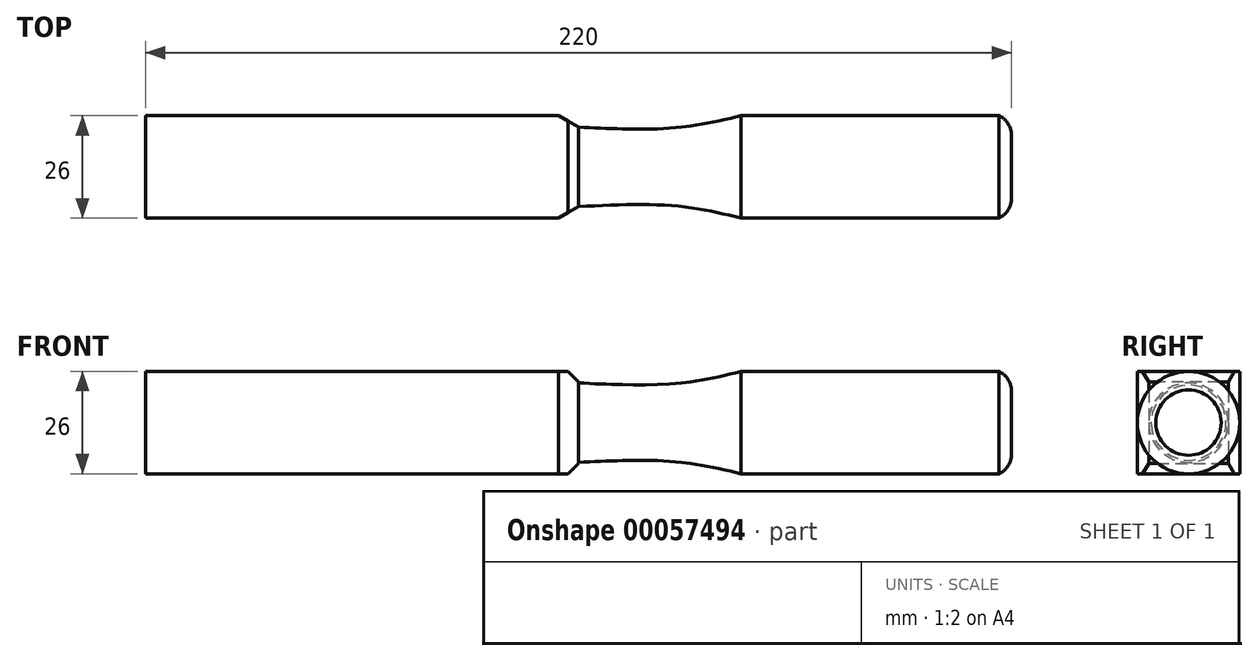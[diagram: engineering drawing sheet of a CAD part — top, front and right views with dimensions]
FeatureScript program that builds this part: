
annotation { "Feature Type Name" : "Feature", "Feature Type Description" : "" }
export const myFeature = defineFeature(function(context is Context, id is Id, definition is map)
    precondition{}
    {
        {
            var Q0;
            Q0=qCreatedBy(makeId("Top.planeOp"),FACE);
            var sketch = newSketch(context, id + "F0", { "sketchPlane" : qUnion([Q0])});
            skLineSegment(sketch, "E0", {"start": v(-89.28, 0) * mm, "end": v(131.67, 0) * mm, "construction": true});
            skLineSegment(sketch, "E1", {"start": v(0, 12.04) * mm, "end": v(0, -13) * mm, "construction": true});
            skLineSegment(sketch, "E2.0", {"start": v(-89.28, -13) * mm, "end": v(131.67, -13) * mm, "construction": true});
            skLineSegment(sketch, "E3.0", {"start": v(-89.28, 13) * mm, "end": v(131.67, 13) * mm, "construction": true});
            skLineSegment(sketch, "E4", {"start": v(0, 13) * mm, "end": v(0, -13) * mm});
            skLineSegment(sketch, "E5.0", {"start": v(-110, 13) * mm, "end": v(-110, -13) * mm});
            skLineSegment(sketch, "E6.0", {"start": v(110, 13) * mm, "end": v(110, -13) * mm});
            skLineSegment(sketch, "E7", {"start": v(-110, -13) * mm, "end": v(0, -13) * mm});
            skLineSegment(sketch, "E8", {"start": v(0, 13) * mm, "end": v(-110, 13) * mm});
            skFitSpline(sketch, "E9", {"points": [v(0, -10.1) * mm, v(24.61, -9.92) * mm, v(41.35, -13) * mm], "startDerivative": vector(47.32, 2.24) * mm, "endDerivative": vector(35, -8.38) * mm});
            skArc(sketch, "E10", {"start": v(106.8, -13) * mm, "mid": v(109.18, -10.95) * mm, "end": v(110, -7.92) * mm});
            skLineSegment(sketch, "E11", {"start": v(41.35, -13) * mm, "end": v(106.8, -13) * mm});
            skLineSegment(sketch, "E12", {"start": v(0, 0) * mm, "end": v(110, 0) * mm});
            skLineSegment(sketch, "E13.0", {"start": v(-5, 13) * mm, "end": v(-5, -13) * mm});
            skLineSegment(sketch, "E14", {"start": v(0, -10.1) * mm, "end": v(-5, -13) * mm});
            skLineSegment(sketch, "E15.MirrorCS", {"start": v(0, 10.1) * mm, "end": v(-5, 13) * mm});
            skSolve(sketch);
        }
        {
            var Q0;
            {var subQ0=sQuery(id+"F0.wireOp",EDGE,"E9");Q0=makeQuery(id+"F0.imprint","IMPRINT",FACE,{"disambiguationData":[TD([[makeQuery(id+"F0.imprint","IMPRINT",EDGE,{"derivedFrom":subQ0}),1.0]])]});}
            var Q1;
            Q1=sQuery(id+"F0.wireOp",EDGE,"E12");
            revolve(context, id + "F1", {"entities" : qUnion([Q0]), "axis" : qUnion([Q1]), "revolveType" : RevolveType.FULL});
        }
        {
            var Q0;
            Q0=makeQuery(id+"F0.imprint","IMPRINT",FACE,{"disambiguationData":[TD([[makeQuery(id+"F0.imprint","IMPRINT",EDGE,{"derivedFrom":sQuery(id+"F0.wireOp",EDGE,"E5.0")}),1.0]])]});
            extrude(context, id + "F2", {"entities" : qUnion([Q0]), "operationType" : NewBodyOperationType.ADD, "depth" : 13 * mm});
        }
        {
            var Q0;
            Q0=makeQuery(id+"F2.opExtrude","CAP_FACE",FACE,{"disambiguationData":[OSD([sQuery(id+"F0.wireOp",EDGE,"E4"),sQuery(id+"F0.wireOp",EDGE,"E5.0"),sQuery(id+"F0.wireOp",EDGE,"E7"),sQuery(id+"F0.wireOp",EDGE,"E8")])],"isStart":true});
            extrude(context, id + "F3", {"entities" : qUnion([Q0]), "operationType" : NewBodyOperationType.ADD, "depth" : 13 * mm});
        }
        {
            var Q0;
            Q0=makeQuery(id+"F0.imprint","IMPRINT",FACE,{"disambiguationData":[TD([[makeQuery(id+"F0.imprint","IMPRINT",EDGE,{"derivedFrom":sQuery(id+"F0.wireOp",EDGE,"E13.0")}),1.0]])]});
            extrude(context, id + "F4", {"entities" : qUnion([Q0]), "depth" : 13 * mm});
        }
        {
            var Q0;
            Q0=makeQuery(id+"F4.opExtrude","CAP_FACE",FACE,{"disambiguationData":[OSD([sQuery(id+"F0.wireOp",EDGE,"E4"),sQuery(id+"F0.wireOp",EDGE,"E13.0"),sQuery(id+"F0.wireOp",EDGE,"E14"),sQuery(id+"F0.wireOp",EDGE,"E15.MirrorCS")])],"isStart":true});
            extrude(context, id + "F5", {"entities" : qUnion([Q0]), "operationType" : NewBodyOperationType.ADD, "depth" : 13 * mm});
        }
        {
            var Q0;
            Q0=makeQuery(id+"F4.opExtrude","CAP_EDGE",EDGE,{"disambiguationData":[OSD([sQuery(id+"F0.wireOp",EDGE,"E4")])],"isStart":false});
            chamfer(context, id + "F6", {"entities" : qUnion([Q0]), "width" : 2.7 * mm, "tangentPropagation" : true});
        }
        {
            var Q0;
            Q0=makeQuery(id+"F5.opExtrude","CAP_EDGE",EDGE,{"disambiguationData":[OSD([sQuery(id+"F0.wireOp",EDGE,"E4")])],"isStart":false});
            chamfer(context, id + "F7", {"entities" : qUnion([Q0]), "width" : 2.7 * mm, "tangentPropagation" : true});
        }
    });
